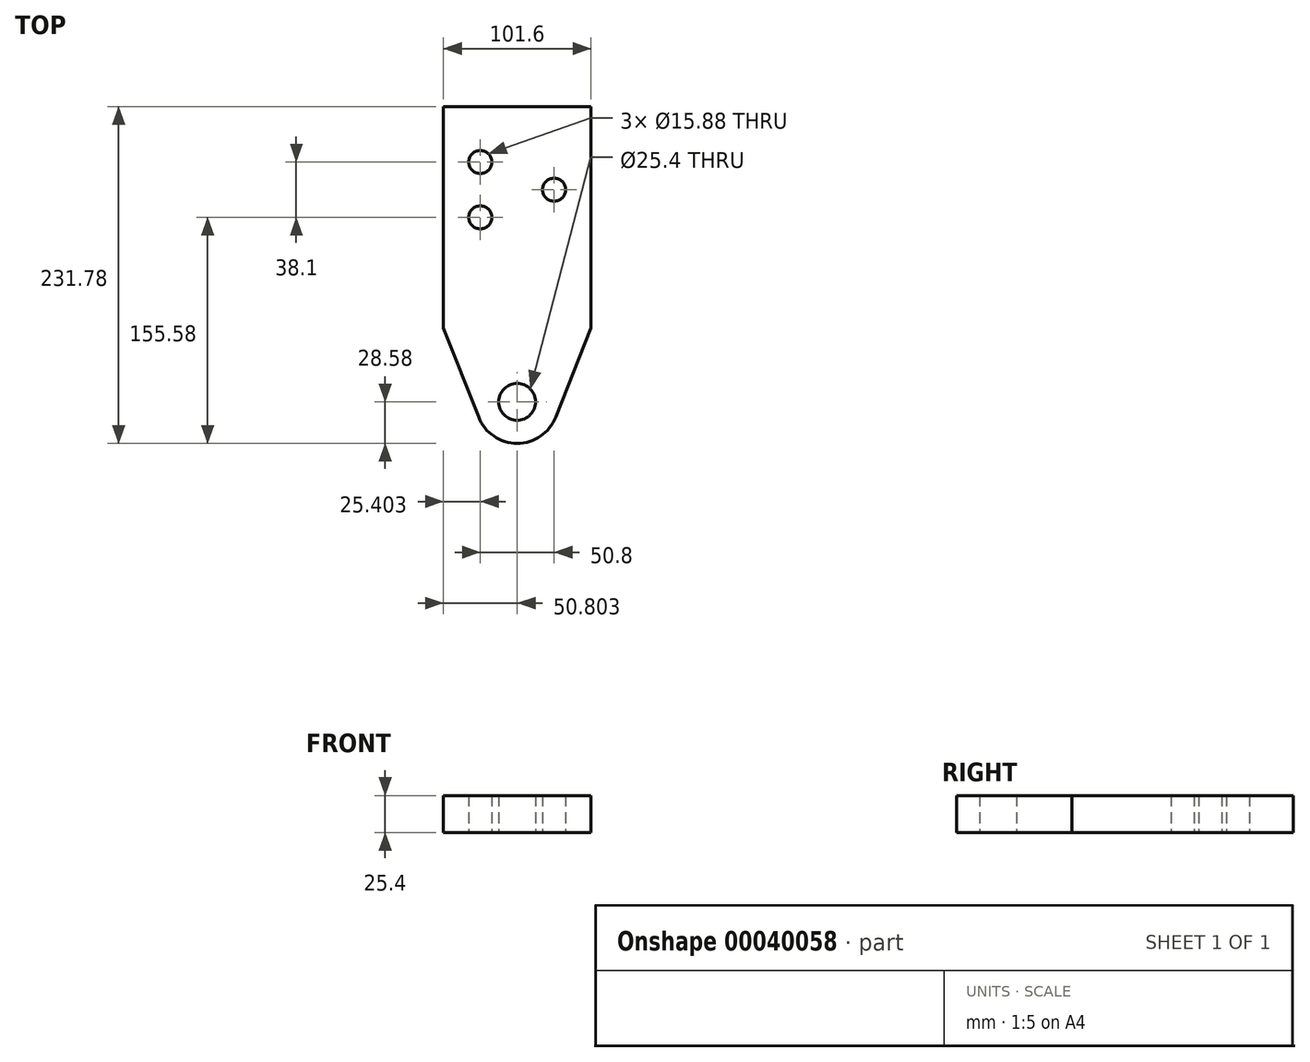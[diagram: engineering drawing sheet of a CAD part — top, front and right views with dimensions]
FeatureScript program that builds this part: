
annotation { "Feature Type Name" : "Feature", "Feature Type Description" : "" }
export const myFeature = defineFeature(function(context is Context, id is Id, definition is map)
    precondition{}
    {
        {
            var Q0;
            Q0=qCreatedBy(makeId("Top.planeOp"),FACE);
            var sketch = newSketch(context, id + "F0", { "sketchPlane" : qUnion([Q0])});
            skLineSegment(sketch, "E0", {"start": v(-62.45, 103.63) * mm, "end": v(39.15, 103.63) * mm});
            skCircle(sketch, "E1", {"center": v(-11.65, -99.57) * mm, "radius": 12.7 * mm});
            skArc(sketch, "E2", {"start": v(-38.22, -110.07) * mm, "mid": v(-11.65, -128.15) * mm, "end": v(14.93, -110.07) * mm});
            skLineSegment(sketch, "E3", {"start": v(-62.45, 103.63) * mm, "end": v(-62.45, -48.77) * mm});
            skLineSegment(sketch, "E4", {"start": v(39.15, 103.63) * mm, "end": v(39.15, -48.77) * mm});
            skLineSegment(sketch, "E5", {"start": v(39.15, -48.77) * mm, "end": v(14.93, -110.07) * mm});
            skLineSegment(sketch, "E6", {"start": v(-62.45, -48.77) * mm, "end": v(-38.22, -110.07) * mm});
            skCircle(sketch, "E7", {"center": v(-37.05, 65.53) * mm, "radius": 7.94 * mm});
            skCircle(sketch, "E8", {"center": v(-37.05, 27.43) * mm, "radius": 7.94 * mm});
            skCircle(sketch, "E9", {"center": v(13.75, 46.48) * mm, "radius": 7.94 * mm});
            skSolve(sketch);
        }
        {
            var Q0;
            Q0=makeQuery(id+"F0.imprint","IMPRINT",FACE,{"disambiguationData":[TD([[makeQuery(id+"F0.imprint","IMPRINT",EDGE,{"derivedFrom":sQuery(id+"F0.wireOp",EDGE,"E0")}),-1.0]])]});
            extrude(context, id + "F1", {"entities" : qUnion([Q0]), "depth" : 25.4 * mm});
        }
    });
